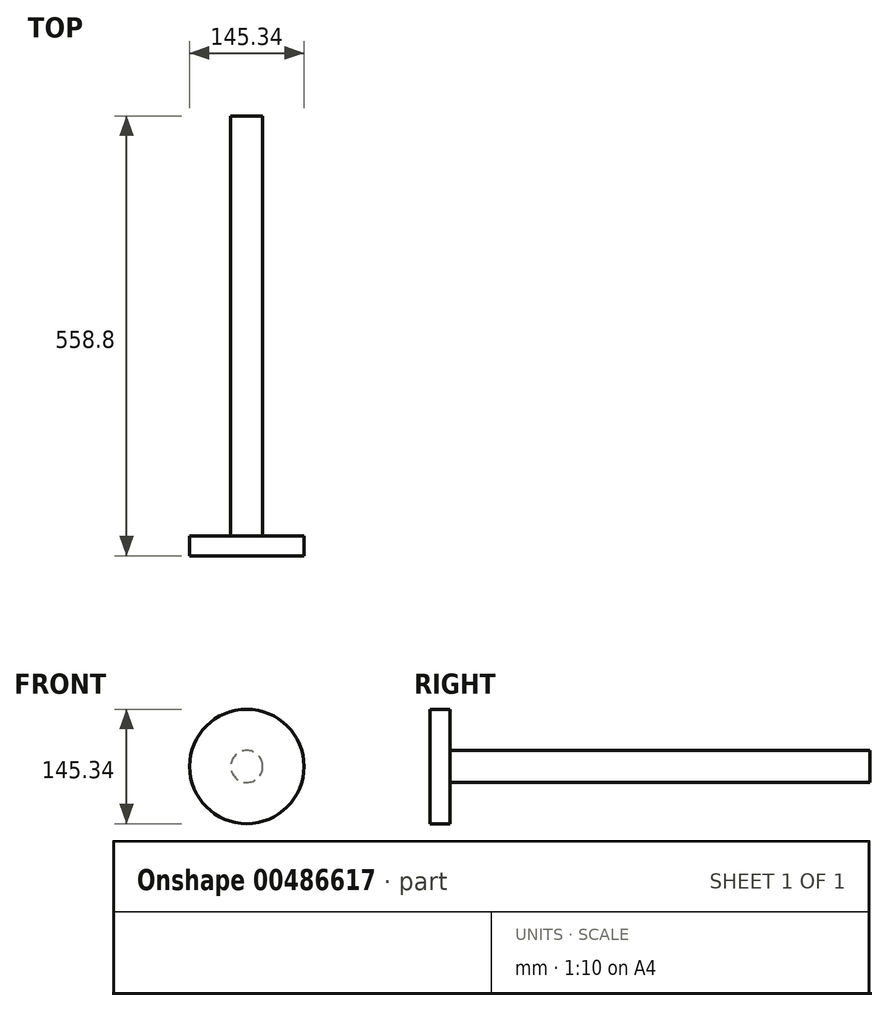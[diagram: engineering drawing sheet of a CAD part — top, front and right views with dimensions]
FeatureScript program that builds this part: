
annotation { "Feature Type Name" : "Feature", "Feature Type Description" : "" }
export const myFeature = defineFeature(function(context is Context, id is Id, definition is map)
    precondition{}
    {
        {
            var Q0;
            Q0=qCreatedBy(makeId("Front.planeOp"),FACE);
            var sketch = newSketch(context, id + "F0", { "sketchPlane" : qUnion([Q0])});
            skCircle(sketch, "E0", {"center": v(0, 0) * mm, "radius": 72.67 * mm});
            skSolve(sketch);
        }
        {
            var Q0;
            Q0 = qSketchRegion(id + "F0", true);
            extrude(context, id + "F1", {"entities" : qUnion([Q0]), "depth" : 25.4 * mm});
        }
        {
            var Q0;
            Q0=qCreatedBy(makeId("Front.planeOp"),FACE);
            var sketch = newSketch(context, id + "F2", { "sketchPlane" : qUnion([Q0])});
            skCircle(sketch, "E1", {"center": v(0, 0) * mm, "radius": 20.34 * mm});
            skSolve(sketch);
        }
        {
            var Q0;
            Q0 = qSketchRegion(id + "F2", true);
            extrude(context, id + "F3", {"entities" : qUnion([Q0]), "operationType" : NewBodyOperationType.ADD, "oppositeDirection" : true, "depth" : 508 * mm});
        }
        {
            var Q0;
            Q0=makeQuery(id+"F3.opExtrude","CAP_FACE",FACE,{"disambiguationData":[OSD([sQuery(id+"F2.wireOp",EDGE,"E1")])],"isStart":false});
            extrude(context, id + "F4", {"entities" : qUnion([Q0]), "operationType" : NewBodyOperationType.ADD, "depth" : 25.4 * mm});
        }
    });
